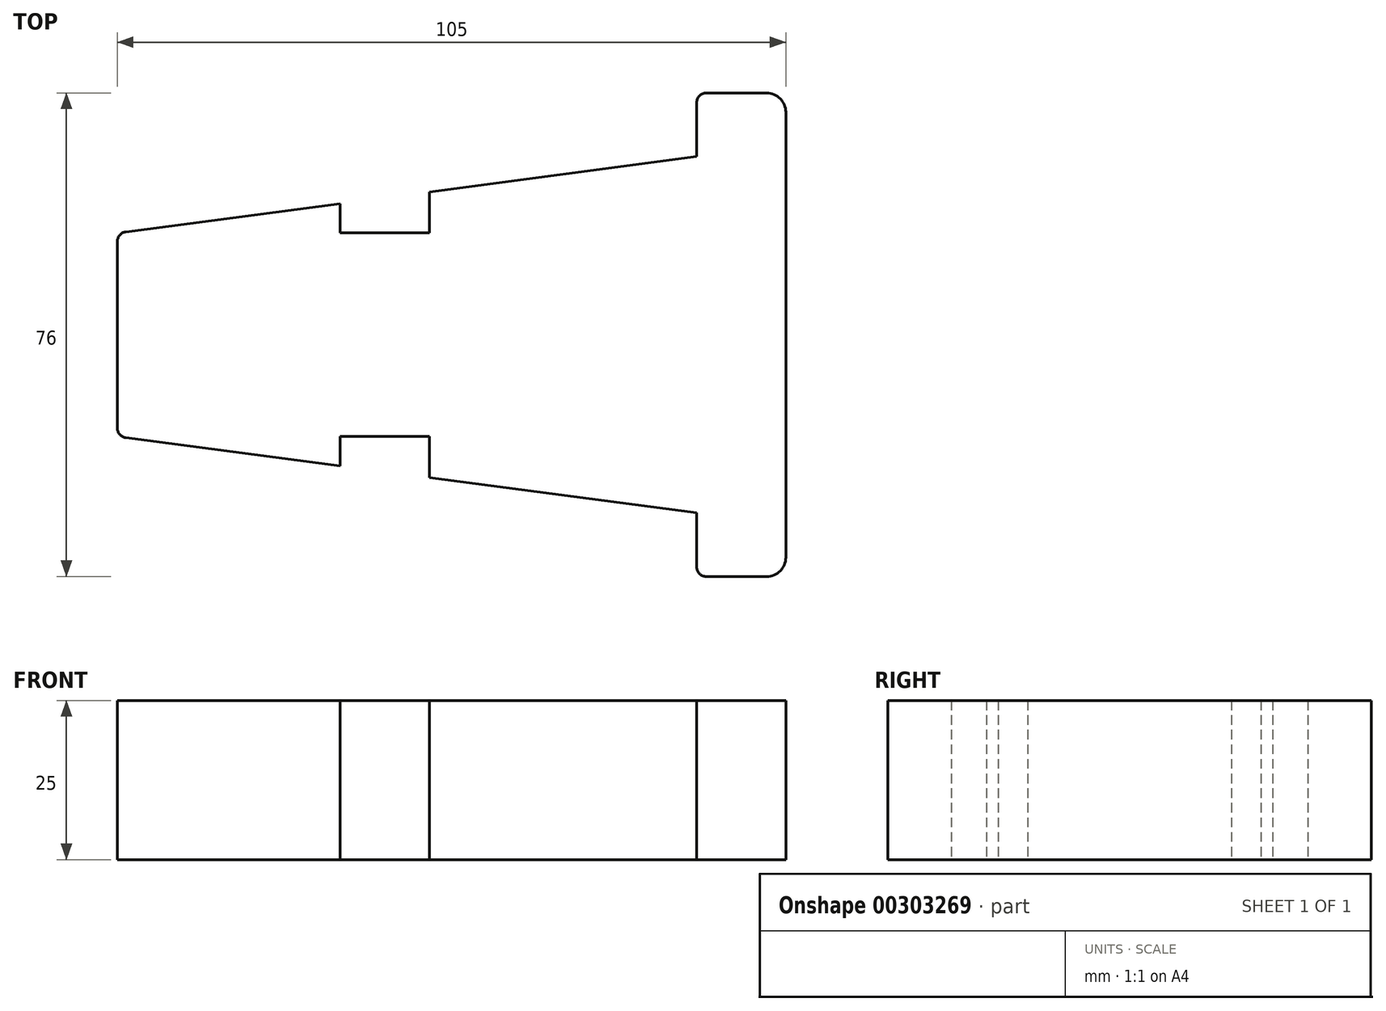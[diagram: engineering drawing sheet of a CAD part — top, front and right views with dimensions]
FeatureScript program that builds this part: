
annotation { "Feature Type Name" : "Feature", "Feature Type Description" : "" }
export const myFeature = defineFeature(function(context is Context, id is Id, definition is map)
    precondition{}
    {
        {
            var Q0;
            Q0=qCreatedBy(makeId("Top.planeOp"),FACE);
            var sketch = newSketch(context, id + "F0", { "sketchPlane" : qUnion([Q0])});
            skLineSegment(sketch, "E0", {"start": v(0, 1.5) * mm, "end": v(0, 32) * mm});
            skLineSegment(sketch, "E1", {"start": v(105, 1.5) * mm, "end": v(105, 51) * mm});
            skLineSegment(sketch, "E2", {"start": v(102, 54) * mm, "end": v(92.5, 54) * mm});
            skLineSegment(sketch, "E3", {"start": v(91, 52.5) * mm, "end": v(91, 44) * mm});
            skLineSegment(sketch, "E4", {"start": v(91, 44) * mm, "end": v(49, 38.46) * mm});
            skLineSegment(sketch, "E5", {"start": v(0, 32) * mm, "end": v(35, 36.62) * mm});
            skLineSegment(sketch, "E6", {"start": v(35, 32) * mm, "end": v(49, 32) * mm});
            skLineSegment(sketch, "E7", {"start": v(49, 32) * mm, "end": v(49, 38.46) * mm});
            skLineSegment(sketch, "E8", {"start": v(35, 32) * mm, "end": v(35, 36.62) * mm});
            skLineSegment(sketch, "E9.trimOffspring", {"start": v(35, 36.62) * mm, "end": v(0, 32) * mm});
            skPoint(sketch, "E10.visualSharp", {"position": v(0, 0) * mm});
            skPoint(sketch, "E11.visualSharp", {"position": v(105, 0) * mm});
            skPoint(sketch, "E12.visualSharp", {"position": v(91, 54) * mm});
            skArc(sketch, "E12.filletArc", {"start": v(92.5, 54) * mm, "mid": v(91.44, 53.56) * mm, "end": v(91, 52.5) * mm});
            skPoint(sketch, "E13.visualSharp", {"position": v(105, 54) * mm});
            skArc(sketch, "E13.filletArc", {"start": v(105, 51) * mm, "mid": v(104.12, 53.12) * mm, "end": v(102, 54) * mm});
            skLineSegment(sketch, "E14", {"start": v(105, 54) * mm, "end": v(105, -19) * mm});
            skLineSegment(sketch, "E15", {"start": v(0, 1.5) * mm, "end": v(0, 1.32) * mm});
            skLineSegment(sketch, "E16", {"start": v(105, 1.5) * mm, "end": v(105, 0) * mm});
            skLineSegment(sketch, "E17", {"start": v(49, 0) * mm, "end": v(35, 0) * mm});
            skLineSegment(sketch, "E18", {"start": v(102, -22) * mm, "end": v(92.5, -22) * mm});
            skLineSegment(sketch, "E19", {"start": v(91, -20.5) * mm, "end": v(91, -12) * mm});
            skLineSegment(sketch, "E20", {"start": v(91, -12) * mm, "end": v(49, -6.46) * mm});
            skLineSegment(sketch, "E21", {"start": v(35, 0) * mm, "end": v(35, -4.62) * mm});
            skLineSegment(sketch, "E22", {"start": v(49, 0) * mm, "end": v(49, -6.46) * mm});
            skPoint(sketch, "E23.visualSharp", {"position": v(91, -22) * mm});
            skArc(sketch, "E23.filletArc", {"start": v(91, -20.5) * mm, "mid": v(91.44, -21.56) * mm, "end": v(92.5, -22) * mm});
            skArc(sketch, "E24.filletArc", {"start": v(0, 1.32) * mm, "mid": v(0.37, 0.33) * mm, "end": v(1.3, -0.17) * mm});
            skPoint(sketch, "E25.visualSharp", {"position": v(105, -22) * mm});
            skArc(sketch, "E25.filletArc", {"start": v(102, -22) * mm, "mid": v(104.12, -21.12) * mm, "end": v(105, -19) * mm});
            skLineSegment(sketch, "E26.trimOffspring", {"start": v(35, -4.62) * mm, "end": v(1.3, -0.17) * mm});
            skSolve(sketch);
        }
        {
            var Q0;
            Q0 = qSketchRegion(id + "F0", true);
            extrude(context, id + "F1", {"entities" : qUnion([Q0]), "depth" : 25 * mm});
        }
        {
            var Q0;
            Q0=makeQuery(id+"F1.opExtrude","SWEPT_EDGE",EDGE,{"disambiguationData":[OSD([sQuery(id+"F0.wireOp",EDGE,"E0"),sQuery(id+"F0.wireOp",EDGE,"E9.trimOffspring")])]});
            fillet(context, id + "F2", {"entities" : qUnion([Q0]), "radius" : 1.5 * mm, "tangentPropagation" : true, "allowEdgeOverflow" : false});
        }
    });
